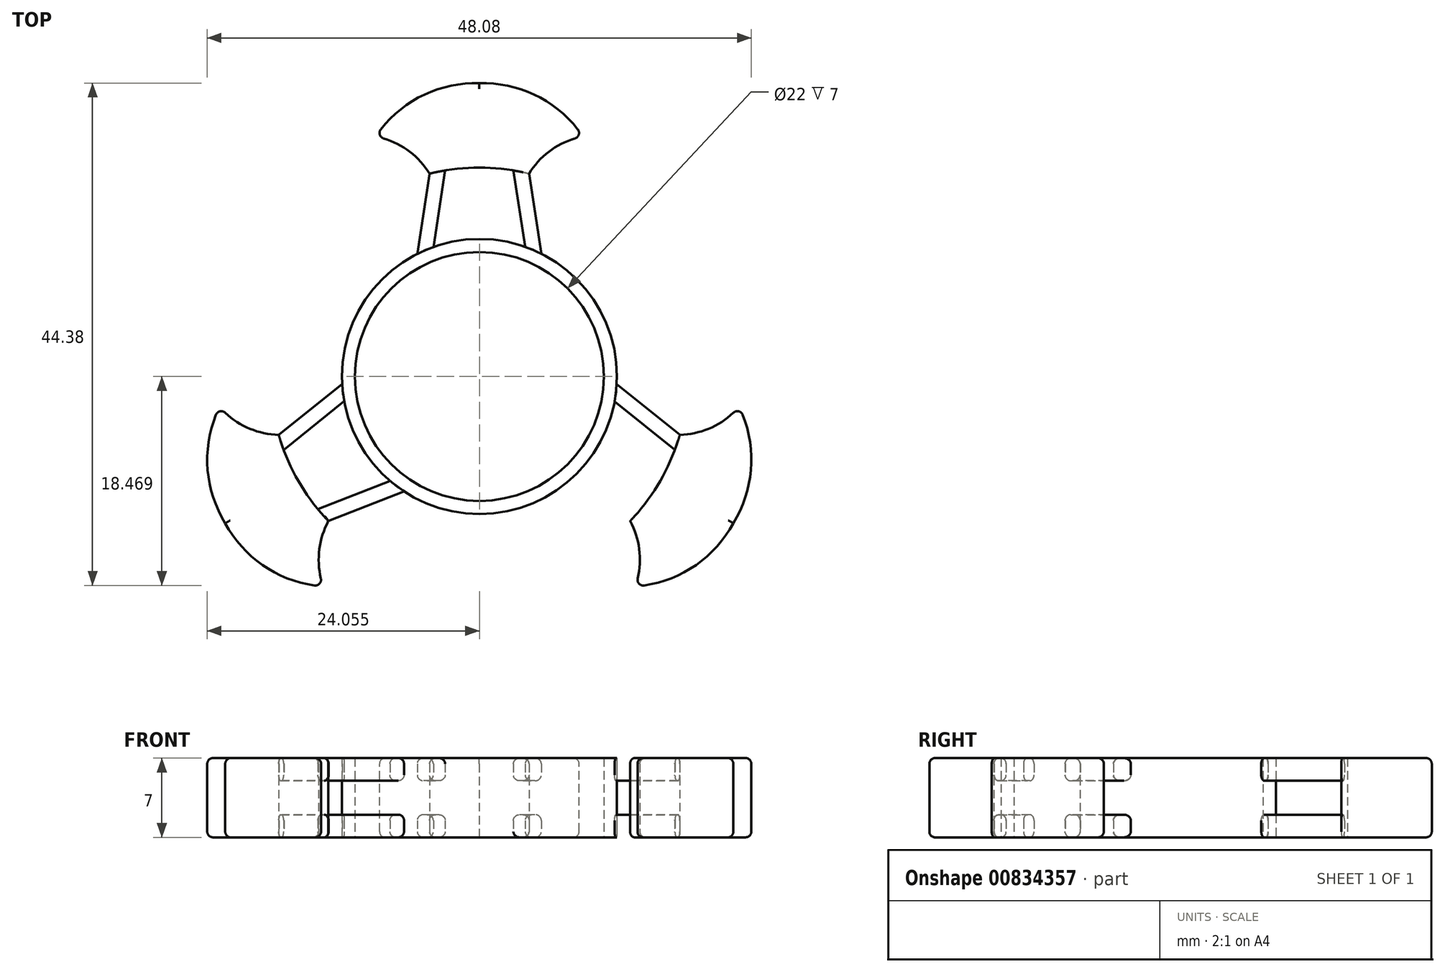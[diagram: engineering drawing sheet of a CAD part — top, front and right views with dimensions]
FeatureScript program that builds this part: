
annotation { "Feature Type Name" : "Feature", "Feature Type Description" : "" }
export const myFeature = defineFeature(function(context is Context, id is Id, definition is map)
    precondition{}
    {
        {
            var Q0;
            Q0=qCreatedBy(makeId("Top.planeOp"),FACE);
            var sketch = newSketch(context, id + "F0", { "sketchPlane" : qUnion([Q0])});
            skArc(sketch, "E0", {"start": v(9.16, 21.21) * mm, "mid": v(5.19, 24.74) * mm, "end": v(0, 25.91) * mm});
            skArc(sketch, "E1", {"start": v(9.16, 21.21) * mm, "mid": v(6.43, 20.07) * mm, "end": v(4.4, 17.93) * mm});
            skArc(sketch, "E2.MirrorCS", {"start": v(-9.16, 21.21) * mm, "mid": v(-6.43, 20.07) * mm, "end": v(-4.4, 17.93) * mm});
            skArc(sketch, "E3.MirrorCS", {"start": v(-9.16, 21.21) * mm, "mid": v(-5.19, 24.74) * mm, "end": v(0, 25.91) * mm});
            skArc(sketch, "E4", {"start": v(4.4, 17.93) * mm, "mid": v(0, 18.45) * mm, "end": v(-4.4, 17.93) * mm});
            skArc(sketch, "E5.MirrorCS", {"start": v(13.8, -18.54) * mm, "mid": v(18.84, -16.86) * mm, "end": v(22.44, -12.96) * mm});
            skArc(sketch, "E6.MirrorCS", {"start": v(22.95, -2.67) * mm, "mid": v(24.02, -7.88) * mm, "end": v(22.44, -12.96) * mm});
            skArc(sketch, "E7.MirrorCS", {"start": v(22.95, -2.67) * mm, "mid": v(20.6, -4.46) * mm, "end": v(17.72, -5.16) * mm});
            skArc(sketch, "E8.MirrorCS", {"start": v(13.8, -18.54) * mm, "mid": v(14.16, -15.6) * mm, "end": v(13.33, -12.77) * mm});
            skArc(sketch, "E9.MirrorCS", {"start": v(17.72, -5.16) * mm, "mid": v(15.98, -9.23) * mm, "end": v(13.33, -12.77) * mm});
            skArc(sketch, "E10.MirrorCS", {"start": v(-17.72, -5.16) * mm, "mid": v(-15.98, -9.23) * mm, "end": v(-13.33, -12.77) * mm});
            skArc(sketch, "E11.MirrorCS", {"start": v(-22.95, -2.67) * mm, "mid": v(-20.6, -4.46) * mm, "end": v(-17.72, -5.16) * mm});
            skArc(sketch, "E12.MirrorCS", {"start": v(-22.95, -2.67) * mm, "mid": v(-24.02, -7.88) * mm, "end": v(-22.44, -12.96) * mm});
            skArc(sketch, "E13.MirrorCS", {"start": v(-13.8, -18.54) * mm, "mid": v(-14.16, -15.6) * mm, "end": v(-13.33, -12.77) * mm});
            skArc(sketch, "E14.MirrorCS", {"start": v(-13.8, -18.54) * mm, "mid": v(-18.84, -16.86) * mm, "end": v(-22.44, -12.96) * mm});
            skLineSegment(sketch, "E15", {"start": v(8.04, -4.26) * mm, "end": v(8.02, -4.24) * mm});
            skLineSegment(sketch, "E16", {"start": v(7.72, -4.81) * mm, "end": v(7.7, -4.8) * mm});
            skLineSegment(sketch, "E17", {"start": v(-14.25, -11.7) * mm, "end": v(-14.27, -11.7) * mm});
            skLineSegment(sketch, "E18", {"start": v(9.09, 0.13) * mm, "end": v(9.06, 0.15) * mm});
            skLineSegment(sketch, "E19", {"start": v(4.64, 7.81) * mm, "end": v(4.65, 7.78) * mm});
            skCircle(sketch, "E20", {"center": v(0.01, 0) * mm, "radius": 11 * mm});
            skCircle(sketch, "E21", {"center": v(0.01, 0) * mm, "radius": 12.15 * mm});
            skLineSegment(sketch, "E22", {"start": v(-4.4, 17.93) * mm, "end": v(-5.48, 10.84) * mm});
            skLineSegment(sketch, "E23", {"start": v(-4.05, 11.45) * mm, "end": v(-3.02, 18.2) * mm});
            skLineSegment(sketch, "E24.MirrorCS", {"start": v(4.05, 11.45) * mm, "end": v(3.02, 18.2) * mm});
            skLineSegment(sketch, "E25.MirrorCS", {"start": v(4.4, 17.93) * mm, "end": v(5.48, 10.84) * mm});
            skLineSegment(sketch, "E26.MirrorCS", {"start": v(-11.93, -2.19) * mm, "end": v(-17.26, -6.47) * mm});
            skLineSegment(sketch, "E27.MirrorCS", {"start": v(-17.7, -5.13) * mm, "end": v(-12.11, -0.65) * mm});
            skLineSegment(sketch, "E28.MirrorCS", {"start": v(-7.88, -9.21) * mm, "end": v(-14.24, -11.69) * mm});
            skLineSegment(sketch, "E29.MirrorCS", {"start": v(-13.31, -12.74) * mm, "end": v(-6.63, -10.14) * mm});
            skLineSegment(sketch, "E30", {"start": v(-14.24, -11.69) * mm, "end": v(-14.25, -11.7) * mm});
            skLineSegment(sketch, "E31", {"start": v(-13.31, -12.74) * mm, "end": v(-13.33, -12.77) * mm});
            skLineSegment(sketch, "E32", {"start": v(-17.26, -6.47) * mm, "end": v(-17.28, -6.48) * mm});
            skLineSegment(sketch, "E33", {"start": v(-17.7, -5.13) * mm, "end": v(-17.72, -5.16) * mm});
            skLineSegment(sketch, "E34.MirrorCS", {"start": v(11.93, -2.19) * mm, "end": v(17.26, -6.47) * mm});
            skLineSegment(sketch, "E35.MirrorCS", {"start": v(17.7, -5.13) * mm, "end": v(12.11, -0.65) * mm});
            skLineSegment(sketch, "E36.MirrorCS", {"start": v(7.88, -9.21) * mm, "end": v(14.24, -11.69) * mm});
            skLineSegment(sketch, "E37.MirrorCS", {"start": v(13.31, -12.74) * mm, "end": v(6.63, -10.14) * mm});
            skLineSegment(sketch, "E38", {"start": v(13.31, -12.74) * mm, "end": v(13.33, -12.77) * mm});
            skLineSegment(sketch, "E39", {"start": v(14.24, -11.69) * mm, "end": v(14.26, -11.7) * mm});
            skLineSegment(sketch, "E40.MirrorCS", {"start": v(14.25, -11.7) * mm, "end": v(14.27, -11.7) * mm});
            skLineSegment(sketch, "E41.MirrorCS", {"start": v(14.24, -11.69) * mm, "end": v(14.25, -11.7) * mm});
            skLineSegment(sketch, "E42.MirrorCS", {"start": v(17.26, -6.47) * mm, "end": v(17.28, -6.48) * mm});
            skLineSegment(sketch, "E43.MirrorCS", {"start": v(17.7, -5.13) * mm, "end": v(17.72, -5.16) * mm});
            skSolve(sketch);
        }
        {
            var Q0;
            Q0=makeQuery(id+"F0.imprint","IMPRINT",FACE,{"disambiguationData":[TD([[makeQuery(id+"F0.imprint","IMPRINT",EDGE,{"derivedFrom":sQuery(id+"F0.wireOp",EDGE,"E0")}),1.0]])]});
            var Q1;
            Q1=makeQuery(id+"F0.imprint","IMPRINT",FACE,{"disambiguationData":[TD([[makeQuery(id+"F0.imprint","IMPRINT",EDGE,{"derivedFrom":sQuery(id+"F0.wireOp",EDGE,"E5.MirrorCS")}),1.0]])]});
            var Q2;
            {var subQ0=sQuery(id+"F0.wireOp",EDGE,"E11.MirrorCS");Q2=makeQuery(id+"F0.imprint","IMPRINT",FACE,{"disambiguationData":[TD([[makeQuery(id+"F0.imprint","IMPRINT",EDGE,{"derivedFrom":subQ0}),-1.0]])]});}
            var Q3;
            Q3=makeQuery(id+"F0.imprint","IMPRINT",FACE,{"disambiguationData":[TD([[makeQuery(id+"F0.imprint","IMPRINT",EDGE,{"derivedFrom":sQuery(id+"F0.wireOp",EDGE,"E20")}),-1.0]])]});
            extrude(context, id + "F1", {"entities" : qUnion([Q0, Q1, Q2, Q3]), "depth" : 7 * mm, "offsetDistance" : 25.4 * mm});
        }
        {
            var Q0;
            Q0=makeQuery(id+"F1.opExtrude","CAP_EDGE",EDGE,{"disambiguationData":[OSD([sQuery(id+"F0.wireOp",EDGE,"E2.MirrorCS")])],"isStart":false});
            var Q1;
            Q1=makeQuery(id+"F1.opExtrude","CAP_EDGE",EDGE,{"disambiguationData":[OSD([sQuery(id+"F0.wireOp",EDGE,"E2.MirrorCS")])],"isStart":true});
            var Q2;
            Q2=makeQuery(id+"F1.opExtrude","CAP_EDGE",EDGE,{"disambiguationData":[OSD([sQuery(id+"F0.wireOp",EDGE,"E3.MirrorCS")])],"isStart":false});
            var Q3;
            Q3=makeQuery(id+"F1.opExtrude","CAP_EDGE",EDGE,{"disambiguationData":[OSD([sQuery(id+"F0.wireOp",EDGE,"E3.MirrorCS")])],"isStart":true});
            var Q4;
            Q4=makeQuery(id+"F1.opExtrude","CAP_EDGE",EDGE,{"disambiguationData":[OSD([sQuery(id+"F0.wireOp",EDGE,"E0")])],"isStart":false});
            var Q5;
            Q5=makeQuery(id+"F1.opExtrude","CAP_EDGE",EDGE,{"disambiguationData":[OSD([sQuery(id+"F0.wireOp",EDGE,"E1")])],"isStart":false});
            var Q6;
            Q6=makeQuery(id+"F1.opExtrude","CAP_EDGE",EDGE,{"disambiguationData":[OSD([sQuery(id+"F0.wireOp",EDGE,"E1")])],"isStart":true});
            var Q7;
            Q7=makeQuery(id+"F1.opExtrude","CAP_EDGE",EDGE,{"disambiguationData":[OSD([sQuery(id+"F0.wireOp",EDGE,"E0")])],"isStart":true});
            var Q8;
            Q8=makeQuery(id+"F1.opExtrude","SWEPT_EDGE",EDGE,{"disambiguationData":[OSD([sQuery(id+"F0.wireOp",EDGE,"E0"),sQuery(id+"F0.wireOp",EDGE,"E1")])]});
            var Q9;
            Q9=makeQuery(id+"F1.opExtrude","SWEPT_EDGE",EDGE,{"disambiguationData":[OSD([sQuery(id+"F0.wireOp",EDGE,"E2.MirrorCS"),sQuery(id+"F0.wireOp",EDGE,"E3.MirrorCS")])]});
            var Q10;
            Q10=makeQuery(id+"F1.opExtrude","CAP_EDGE",EDGE,{"disambiguationData":[OSD([sQuery(id+"F0.wireOp",EDGE,"E7.MirrorCS")])],"isStart":false});
            var Q11;
            Q11=makeQuery(id+"F1.opExtrude","CAP_EDGE",EDGE,{"disambiguationData":[OSD([sQuery(id+"F0.wireOp",EDGE,"E6.MirrorCS")])],"isStart":false});
            var Q12;
            Q12=makeQuery(id+"F1.opExtrude","CAP_EDGE",EDGE,{"disambiguationData":[OSD([sQuery(id+"F0.wireOp",EDGE,"E5.MirrorCS")])],"isStart":false});
            var Q13;
            Q13=makeQuery(id+"F1.opExtrude","CAP_EDGE",EDGE,{"disambiguationData":[OSD([sQuery(id+"F0.wireOp",EDGE,"E8.MirrorCS")])],"isStart":false});
            var Q14;
            Q14=makeQuery(id+"F1.opExtrude","SWEPT_EDGE",EDGE,{"disambiguationData":[OSD([sQuery(id+"F0.wireOp",EDGE,"E5.MirrorCS"),sQuery(id+"F0.wireOp",EDGE,"E8.MirrorCS")])]});
            var Q15;
            Q15=makeQuery(id+"F1.opExtrude","SWEPT_EDGE",EDGE,{"disambiguationData":[OSD([sQuery(id+"F0.wireOp",EDGE,"E6.MirrorCS"),sQuery(id+"F0.wireOp",EDGE,"E7.MirrorCS")])]});
            var Q16;
            Q16=makeQuery(id+"F1.opExtrude","CAP_EDGE",EDGE,{"disambiguationData":[OSD([sQuery(id+"F0.wireOp",EDGE,"E7.MirrorCS")])],"isStart":true});
            var Q17;
            Q17=makeQuery(id+"F1.opExtrude","CAP_EDGE",EDGE,{"disambiguationData":[OSD([sQuery(id+"F0.wireOp",EDGE,"E6.MirrorCS")])],"isStart":true});
            var Q18;
            Q18=makeQuery(id+"F1.opExtrude","CAP_EDGE",EDGE,{"disambiguationData":[OSD([sQuery(id+"F0.wireOp",EDGE,"E8.MirrorCS")])],"isStart":true});
            var Q19;
            Q19=makeQuery(id+"F1.opExtrude","CAP_EDGE",EDGE,{"disambiguationData":[OSD([sQuery(id+"F0.wireOp",EDGE,"E5.MirrorCS")])],"isStart":true});
            var Q20;
            Q20=makeQuery(id+"F1.opExtrude","CAP_EDGE",EDGE,{"disambiguationData":[OSD([sQuery(id+"F0.wireOp",EDGE,"E11.MirrorCS")])],"isStart":false});
            var Q21;
            Q21=makeQuery(id+"F1.opExtrude","CAP_EDGE",EDGE,{"disambiguationData":[OSD([sQuery(id+"F0.wireOp",EDGE,"E12.MirrorCS")])],"isStart":false});
            var Q22;
            Q22=makeQuery(id+"F1.opExtrude","CAP_EDGE",EDGE,{"disambiguationData":[OSD([sQuery(id+"F0.wireOp",EDGE,"E14.MirrorCS")])],"isStart":false});
            var Q23;
            Q23=makeQuery(id+"F1.opExtrude","CAP_EDGE",EDGE,{"disambiguationData":[OSD([sQuery(id+"F0.wireOp",EDGE,"E13.MirrorCS")])],"isStart":false});
            var Q24;
            Q24=makeQuery(id+"F1.opExtrude","SWEPT_EDGE",EDGE,{"disambiguationData":[OSD([sQuery(id+"F0.wireOp",EDGE,"E13.MirrorCS"),sQuery(id+"F0.wireOp",EDGE,"E14.MirrorCS")])]});
            var Q25;
            Q25=makeQuery(id+"F1.opExtrude","CAP_EDGE",EDGE,{"disambiguationData":[OSD([sQuery(id+"F0.wireOp",EDGE,"E13.MirrorCS")])],"isStart":true});
            var Q26;
            Q26=makeQuery(id+"F1.opExtrude","SWEPT_EDGE",EDGE,{"disambiguationData":[OSD([sQuery(id+"F0.wireOp",EDGE,"E11.MirrorCS"),sQuery(id+"F0.wireOp",EDGE,"E12.MirrorCS")])]});
            var Q27;
            Q27=makeQuery(id+"F1.opExtrude","CAP_EDGE",EDGE,{"disambiguationData":[OSD([sQuery(id+"F0.wireOp",EDGE,"E11.MirrorCS")])],"isStart":true});
            var Q28;
            Q28=makeQuery(id+"F1.opExtrude","CAP_EDGE",EDGE,{"disambiguationData":[OSD([sQuery(id+"F0.wireOp",EDGE,"E12.MirrorCS")])],"isStart":true});
            var Q29;
            Q29=makeQuery(id+"F1.opExtrude","CAP_EDGE",EDGE,{"disambiguationData":[OSD([sQuery(id+"F0.wireOp",EDGE,"E14.MirrorCS")])],"isStart":true});
            fillet(context, id + "F2", {"entities" : qUnion([Q0, Q1, Q2, Q3, Q4, Q5, Q6, Q7, Q8, Q9, Q10, Q11, Q12, Q13, Q14, Q15, Q16, Q17, Q18, Q19, Q20, Q21, Q22, Q23, Q24, Q25, Q26, Q27, Q28, Q29]), "radius" : 0.5 * mm, "tangentPropagation" : true, "allowEdgeOverflow" : false});
        }
        {
            var Q0;
            {var subQ0=sQuery(id+"F0.wireOp",EDGE,"E22");Q0=makeQuery(id+"F0.imprint","IMPRINT",FACE,{"disambiguationData":[TD([[makeQuery(id+"F0.imprint","IMPRINT",EDGE,{"derivedFrom":subQ0}),1.0]])]});}
            var Q1;
            {var subQ0=sQuery(id+"F0.wireOp",EDGE,"E25.MirrorCS");var subQ5=sQuery(id+"F0.wireOp",EDGE,"E21");var subQ6=makeQuery(id+"F0.imprint","INTERSECT",VERTEX,{"derivedFrom":[subQ5,subQ0]});Q1=makeQuery(id+"F0.imprint","IMPRINT",FACE,{"disambiguationData":[TD([[makeQuery(id+"F0.imprint","IMPRINT",EDGE,{"disambiguationData":[TD([[subQ6,-1.0]])],"derivedFrom":subQ5}),-1.0]])]});}
            var Q2;
            {var subQ1=sQuery(id+"F0.wireOp",EDGE,"E26.MirrorCS");Q2=makeQuery(id+"F0.imprint","IMPRINT",FACE,{"disambiguationData":[TD([[makeQuery(id+"F0.imprint","IMPRINT",EDGE,{"derivedFrom":subQ1}),-1.0]])]});}
            var Q3;
            {var subQ6=sQuery(id+"F0.wireOp",EDGE,"E17");Q3=makeQuery(id+"F0.imprint","IMPRINT",FACE,{"disambiguationData":[TD([[makeQuery(id+"F0.imprint","IMPRINT",EDGE,{"derivedFrom":subQ6}),1.0]])]});}
            var Q4;
            {var subQ0=sQuery(id+"F0.wireOp",EDGE,"E42.MirrorCS");Q4=makeQuery(id+"F0.imprint","IMPRINT",FACE,{"disambiguationData":[TD([[makeQuery(id+"F0.imprint","IMPRINT",EDGE,{"derivedFrom":subQ0}),1.0]])]});}
            var Q5;
            {var subQ0=sQuery(id+"F0.wireOp",EDGE,"E38");Q5=makeQuery(id+"F0.imprint","IMPRINT",FACE,{"disambiguationData":[TD([[makeQuery(id+"F0.imprint","IMPRINT",EDGE,{"derivedFrom":subQ0}),1.0]])]});}
            extrude(context, id + "F3", {"entities" : qUnion([Q0, Q1, Q2, Q3, Q4, Q5]), "depth" : 2 * mm, "offsetDistance" : 25.4 * mm});
        }
        {
            var Q0;
            Q0=makeQuery(id+"F3.opExtrude","SWEPT_BODY",BODY,{"disambiguationData":[OSD([sQuery(id+"F0.wireOp",EDGE,"E9.MirrorCS"),sQuery(id+"F0.wireOp",EDGE,"E21"),sQuery(id+"F0.wireOp",EDGE,"E36.MirrorCS"),sQuery(id+"F0.wireOp",EDGE,"E37.MirrorCS"),sQuery(id+"F0.wireOp",EDGE,"E38"),sQuery(id+"F0.wireOp",EDGE,"E40.MirrorCS"),sQuery(id+"F0.wireOp",EDGE,"E41.MirrorCS")])]});
            var Q1;
            Q1=makeQuery(id+"F3.opExtrude","SWEPT_BODY",BODY,{"disambiguationData":[OSD([sQuery(id+"F0.wireOp",EDGE,"E10.MirrorCS"),sQuery(id+"F0.wireOp",EDGE,"E17"),sQuery(id+"F0.wireOp",EDGE,"E21"),sQuery(id+"F0.wireOp",EDGE,"E28.MirrorCS"),sQuery(id+"F0.wireOp",EDGE,"E29.MirrorCS"),sQuery(id+"F0.wireOp",EDGE,"E30"),sQuery(id+"F0.wireOp",EDGE,"E31")])]});
            var Q2;
            Q2=makeQuery(id+"F3.opExtrude","SWEPT_BODY",BODY,{"disambiguationData":[OSD([sQuery(id+"F0.wireOp",EDGE,"E10.MirrorCS"),sQuery(id+"F0.wireOp",EDGE,"E21"),sQuery(id+"F0.wireOp",EDGE,"E26.MirrorCS"),sQuery(id+"F0.wireOp",EDGE,"E27.MirrorCS"),sQuery(id+"F0.wireOp",EDGE,"E32"),sQuery(id+"F0.wireOp",EDGE,"E33")])]});
            var Q3;
            Q3=makeQuery(id+"F3.opExtrude","SWEPT_BODY",BODY,{"disambiguationData":[OSD([sQuery(id+"F0.wireOp",EDGE,"E9.MirrorCS"),sQuery(id+"F0.wireOp",EDGE,"E21"),sQuery(id+"F0.wireOp",EDGE,"E34.MirrorCS"),sQuery(id+"F0.wireOp",EDGE,"E35.MirrorCS"),sQuery(id+"F0.wireOp",EDGE,"E42.MirrorCS"),sQuery(id+"F0.wireOp",EDGE,"E43.MirrorCS")])]});
            var Q4;
            Q4=makeQuery(id+"F3.opExtrude","SWEPT_BODY",BODY,{"disambiguationData":[OSD([sQuery(id+"F0.wireOp",EDGE,"E4"),sQuery(id+"F0.wireOp",EDGE,"E21"),sQuery(id+"F0.wireOp",EDGE,"E24.MirrorCS"),sQuery(id+"F0.wireOp",EDGE,"E25.MirrorCS")])]});
            var Q5;
            Q5=makeQuery(id+"F3.opExtrude","SWEPT_BODY",BODY,{"disambiguationData":[OSD([sQuery(id+"F0.wireOp",EDGE,"E4"),sQuery(id+"F0.wireOp",EDGE,"E21"),sQuery(id+"F0.wireOp",EDGE,"E22"),sQuery(id+"F0.wireOp",EDGE,"E23")])]});
            transform(context, id + "F4", {"entities" : qUnion([Q0, Q1, Q2, Q3, Q4, Q5]), "transformType" : TransformType.TRANSLATION_3D, "dx" : 0 * mm, "dy" : 0 * mm, "dz" : 5 * mm, "makeCopy" : false});
        }
        {
            var Q0;
            {var subQ0=sQuery(id+"F0.wireOp",EDGE,"E42.MirrorCS");Q0=makeQuery(id+"F0.imprint","IMPRINT",FACE,{"disambiguationData":[TD([[makeQuery(id+"F0.imprint","IMPRINT",EDGE,{"derivedFrom":subQ0}),1.0]])]});}
            var Q1;
            {var subQ0=sQuery(id+"F0.wireOp",EDGE,"E38");Q1=makeQuery(id+"F0.imprint","IMPRINT",FACE,{"disambiguationData":[TD([[makeQuery(id+"F0.imprint","IMPRINT",EDGE,{"derivedFrom":subQ0}),1.0]])]});}
            var Q2;
            {var subQ6=sQuery(id+"F0.wireOp",EDGE,"E17");Q2=makeQuery(id+"F0.imprint","IMPRINT",FACE,{"disambiguationData":[TD([[makeQuery(id+"F0.imprint","IMPRINT",EDGE,{"derivedFrom":subQ6}),1.0]])]});}
            var Q3;
            {var subQ1=sQuery(id+"F0.wireOp",EDGE,"E26.MirrorCS");Q3=makeQuery(id+"F0.imprint","IMPRINT",FACE,{"disambiguationData":[TD([[makeQuery(id+"F0.imprint","IMPRINT",EDGE,{"derivedFrom":subQ1}),-1.0]])]});}
            var Q4;
            {var subQ0=sQuery(id+"F0.wireOp",EDGE,"E25.MirrorCS");var subQ5=sQuery(id+"F0.wireOp",EDGE,"E21");var subQ6=makeQuery(id+"F0.imprint","INTERSECT",VERTEX,{"derivedFrom":[subQ5,subQ0]});Q4=makeQuery(id+"F0.imprint","IMPRINT",FACE,{"disambiguationData":[TD([[makeQuery(id+"F0.imprint","IMPRINT",EDGE,{"disambiguationData":[TD([[subQ6,-1.0]])],"derivedFrom":subQ5}),-1.0]])]});}
            var Q5;
            {var subQ0=sQuery(id+"F0.wireOp",EDGE,"E22");Q5=makeQuery(id+"F0.imprint","IMPRINT",FACE,{"disambiguationData":[TD([[makeQuery(id+"F0.imprint","IMPRINT",EDGE,{"derivedFrom":subQ0}),1.0]])]});}
            extrude(context, id + "F5", {"entities" : qUnion([Q0, Q1, Q2, Q3, Q4, Q5]), "depth" : 2 * mm, "offsetDistance" : 25.4 * mm});
        }
        {
            var Q0;
            Q0=makeQuery(id+"F3.opExtrude","CAP_EDGE",EDGE,{"disambiguationData":[OSD([sQuery(id+"F0.wireOp",EDGE,"E24.MirrorCS")])],"isStart":true});
            var Q1;
            Q1=makeQuery(id+"F3.opExtrude","CAP_EDGE",EDGE,{"disambiguationData":[OSD([sQuery(id+"F0.wireOp",EDGE,"E24.MirrorCS")])],"isStart":false});
            var Q2;
            Q2=makeQuery(id+"F3.opExtrude","CAP_EDGE",EDGE,{"disambiguationData":[OSD([sQuery(id+"F0.wireOp",EDGE,"E25.MirrorCS")])],"isStart":false});
            var Q3;
            Q3=makeQuery(id+"F3.opExtrude","CAP_EDGE",EDGE,{"disambiguationData":[OSD([sQuery(id+"F0.wireOp",EDGE,"E25.MirrorCS")])],"isStart":true});
            var Q4;
            Q4=makeQuery(id+"F5.opExtrude","CAP_EDGE",EDGE,{"disambiguationData":[OSD([sQuery(id+"F0.wireOp",EDGE,"E24.MirrorCS")])],"isStart":false});
            var Q5;
            Q5=makeQuery(id+"F5.opExtrude","CAP_EDGE",EDGE,{"disambiguationData":[OSD([sQuery(id+"F0.wireOp",EDGE,"E25.MirrorCS")])],"isStart":false});
            var Q6;
            Q6=makeQuery(id+"F3.opExtrude","CAP_EDGE",EDGE,{"disambiguationData":[OSD([sQuery(id+"F0.wireOp",EDGE,"E22")])],"isStart":true});
            var Q7;
            Q7=makeQuery(id+"F3.opExtrude","CAP_EDGE",EDGE,{"disambiguationData":[OSD([sQuery(id+"F0.wireOp",EDGE,"E22")])],"isStart":false});
            var Q8;
            Q8=makeQuery(id+"F3.opExtrude","CAP_EDGE",EDGE,{"disambiguationData":[OSD([sQuery(id+"F0.wireOp",EDGE,"E23")])],"isStart":false});
            var Q9;
            Q9=makeQuery(id+"F3.opExtrude","CAP_EDGE",EDGE,{"disambiguationData":[OSD([sQuery(id+"F0.wireOp",EDGE,"E23")])],"isStart":true});
            var Q10;
            Q10=makeQuery(id+"F5.opExtrude","CAP_EDGE",EDGE,{"disambiguationData":[OSD([sQuery(id+"F0.wireOp",EDGE,"E22")])],"isStart":false});
            var Q11;
            Q11=makeQuery(id+"F5.opExtrude","CAP_EDGE",EDGE,{"disambiguationData":[OSD([sQuery(id+"F0.wireOp",EDGE,"E37.MirrorCS")])],"isStart":false});
            var Q12;
            Q12=makeQuery(id+"F3.opExtrude","CAP_EDGE",EDGE,{"disambiguationData":[OSD([sQuery(id+"F0.wireOp",EDGE,"E37.MirrorCS")])],"isStart":false});
            var Q13;
            Q13=makeQuery(id+"F3.opExtrude","CAP_EDGE",EDGE,{"disambiguationData":[OSD([sQuery(id+"F0.wireOp",EDGE,"E37.MirrorCS")])],"isStart":true});
            var Q14;
            Q14=makeQuery(id+"F5.opExtrude","CAP_EDGE",EDGE,{"disambiguationData":[OSD([sQuery(id+"F0.wireOp",EDGE,"E34.MirrorCS")])],"isStart":false});
            var Q15;
            Q15=makeQuery(id+"F3.opExtrude","CAP_EDGE",EDGE,{"disambiguationData":[OSD([sQuery(id+"F0.wireOp",EDGE,"E36.MirrorCS")])],"isStart":false});
            var Q16;
            Q16=makeQuery(id+"F3.opExtrude","CAP_EDGE",EDGE,{"disambiguationData":[OSD([sQuery(id+"F0.wireOp",EDGE,"E36.MirrorCS")])],"isStart":true});
            var Q17;
            Q17=makeQuery(id+"F5.opExtrude","CAP_EDGE",EDGE,{"disambiguationData":[OSD([sQuery(id+"F0.wireOp",EDGE,"E36.MirrorCS")])],"isStart":false});
            var Q18;
            Q18=makeQuery(id+"F3.opExtrude","CAP_EDGE",EDGE,{"disambiguationData":[OSD([sQuery(id+"F0.wireOp",EDGE,"E35.MirrorCS")])],"isStart":true});
            var Q19;
            Q19=makeQuery(id+"F3.opExtrude","CAP_EDGE",EDGE,{"disambiguationData":[OSD([sQuery(id+"F0.wireOp",EDGE,"E35.MirrorCS")])],"isStart":false});
            var Q20;
            Q20=makeQuery(id+"F5.opExtrude","CAP_EDGE",EDGE,{"disambiguationData":[OSD([sQuery(id+"F0.wireOp",EDGE,"E35.MirrorCS")])],"isStart":false});
            var Q21;
            Q21=makeQuery(id+"F3.opExtrude","CAP_EDGE",EDGE,{"disambiguationData":[OSD([sQuery(id+"F0.wireOp",EDGE,"E34.MirrorCS")])],"isStart":true});
            var Q22;
            Q22=makeQuery(id+"F3.opExtrude","CAP_EDGE",EDGE,{"disambiguationData":[OSD([sQuery(id+"F0.wireOp",EDGE,"E34.MirrorCS")])],"isStart":false});
            var Q23;
            Q23=makeQuery(id+"F3.opExtrude","CAP_EDGE",EDGE,{"disambiguationData":[OSD([sQuery(id+"F0.wireOp",EDGE,"E29.MirrorCS")])],"isStart":false});
            var Q24;
            Q24=makeQuery(id+"F3.opExtrude","CAP_EDGE",EDGE,{"disambiguationData":[OSD([sQuery(id+"F0.wireOp",EDGE,"E28.MirrorCS")])],"isStart":false});
            var Q25;
            Q25=makeQuery(id+"F3.opExtrude","CAP_EDGE",EDGE,{"disambiguationData":[OSD([sQuery(id+"F0.wireOp",EDGE,"E27.MirrorCS")])],"isStart":false});
            var Q26;
            Q26=makeQuery(id+"F3.opExtrude","CAP_EDGE",EDGE,{"disambiguationData":[OSD([sQuery(id+"F0.wireOp",EDGE,"E26.MirrorCS")])],"isStart":false});
            var Q27;
            Q27=makeQuery(id+"F5.opExtrude","CAP_EDGE",EDGE,{"disambiguationData":[OSD([sQuery(id+"F0.wireOp",EDGE,"E28.MirrorCS")])],"isStart":false});
            var Q28;
            Q28=makeQuery(id+"F5.opExtrude","CAP_EDGE",EDGE,{"disambiguationData":[OSD([sQuery(id+"F0.wireOp",EDGE,"E29.MirrorCS")])],"isStart":false});
            var Q29;
            Q29=makeQuery(id+"F3.opExtrude","CAP_EDGE",EDGE,{"disambiguationData":[OSD([sQuery(id+"F0.wireOp",EDGE,"E28.MirrorCS")])],"isStart":true});
            var Q30;
            Q30=makeQuery(id+"F3.opExtrude","CAP_EDGE",EDGE,{"disambiguationData":[OSD([sQuery(id+"F0.wireOp",EDGE,"E29.MirrorCS")])],"isStart":true});
            var Q31;
            Q31=makeQuery(id+"F5.opExtrude","CAP_EDGE",EDGE,{"disambiguationData":[OSD([sQuery(id+"F0.wireOp",EDGE,"E27.MirrorCS")])],"isStart":false});
            var Q32;
            Q32=makeQuery(id+"F3.opExtrude","CAP_EDGE",EDGE,{"disambiguationData":[OSD([sQuery(id+"F0.wireOp",EDGE,"E26.MirrorCS")])],"isStart":true});
            var Q33;
            Q33=makeQuery(id+"F5.opExtrude","CAP_EDGE",EDGE,{"disambiguationData":[OSD([sQuery(id+"F0.wireOp",EDGE,"E26.MirrorCS")])],"isStart":false});
            var Q34;
            Q34=makeQuery(id+"F3.opExtrude","CAP_EDGE",EDGE,{"disambiguationData":[OSD([sQuery(id+"F0.wireOp",EDGE,"E27.MirrorCS")])],"isStart":true});
            var Q35;
            Q35=makeQuery(id+"F3.opExtrude","CAP_EDGE",EDGE,{"disambiguationData":[OSD([sQuery(id+"F0.wireOp",EDGE,"E38")])],"isStart":false});
            var Q36;
            Q36=makeQuery(id+"F5.opExtrude","CAP_EDGE",EDGE,{"disambiguationData":[OSD([sQuery(id+"F0.wireOp",EDGE,"E38")])],"isStart":false});
            var Q37;
            Q37=makeQuery(id+"F5.opExtrude","CAP_EDGE",EDGE,{"disambiguationData":[OSD([sQuery(id+"F0.wireOp",EDGE,"E36.MirrorCS")])],"isStart":true});
            var Q38;
            Q38=makeQuery(id+"F5.opExtrude","CAP_EDGE",EDGE,{"disambiguationData":[OSD([sQuery(id+"F0.wireOp",EDGE,"E37.MirrorCS")])],"isStart":true});
            var Q39;
            Q39=makeQuery(id+"F5.opExtrude","CAP_EDGE",EDGE,{"disambiguationData":[OSD([sQuery(id+"F0.wireOp",EDGE,"E38")])],"isStart":true});
            var Q40;
            Q40=makeQuery(id+"F3.opExtrude","CAP_EDGE",EDGE,{"disambiguationData":[OSD([sQuery(id+"F0.wireOp",EDGE,"E38")])],"isStart":true});
            var Q41;
            Q41=makeQuery(id+"F5.opExtrude","CAP_EDGE",EDGE,{"disambiguationData":[OSD([sQuery(id+"F0.wireOp",EDGE,"E34.MirrorCS")])],"isStart":true});
            var Q42;
            Q42=makeQuery(id+"F5.opExtrude","CAP_EDGE",EDGE,{"disambiguationData":[OSD([sQuery(id+"F0.wireOp",EDGE,"E35.MirrorCS")])],"isStart":true});
            var Q43;
            Q43=makeQuery(id+"F5.opExtrude","CAP_EDGE",EDGE,{"disambiguationData":[OSD([sQuery(id+"F0.wireOp",EDGE,"E29.MirrorCS")])],"isStart":true});
            var Q44;
            Q44=makeQuery(id+"F5.opExtrude","CAP_EDGE",EDGE,{"disambiguationData":[OSD([sQuery(id+"F0.wireOp",EDGE,"E28.MirrorCS")])],"isStart":true});
            var Q45;
            Q45=makeQuery(id+"F5.opExtrude","CAP_EDGE",EDGE,{"disambiguationData":[OSD([sQuery(id+"F0.wireOp",EDGE,"E31")])],"isStart":false});
            var Q46;
            Q46=makeQuery(id+"F5.opExtrude","CAP_EDGE",EDGE,{"disambiguationData":[OSD([sQuery(id+"F0.wireOp",EDGE,"E31")])],"isStart":true});
            var Q47;
            Q47=makeQuery(id+"F3.opExtrude","CAP_EDGE",EDGE,{"disambiguationData":[OSD([sQuery(id+"F0.wireOp",EDGE,"E31")])],"isStart":false});
            var Q48;
            Q48=makeQuery(id+"F3.opExtrude","CAP_EDGE",EDGE,{"disambiguationData":[OSD([sQuery(id+"F0.wireOp",EDGE,"E31")])],"isStart":true});
            var Q49;
            Q49=makeQuery(id+"F5.opExtrude","CAP_EDGE",EDGE,{"disambiguationData":[OSD([sQuery(id+"F0.wireOp",EDGE,"E27.MirrorCS")])],"isStart":true});
            var Q50;
            Q50=makeQuery(id+"F5.opExtrude","CAP_EDGE",EDGE,{"disambiguationData":[OSD([sQuery(id+"F0.wireOp",EDGE,"E26.MirrorCS")])],"isStart":true});
            var Q51;
            Q51=makeQuery(id+"F5.opExtrude","CAP_EDGE",EDGE,{"disambiguationData":[OSD([sQuery(id+"F0.wireOp",EDGE,"E23")])],"isStart":true});
            var Q52;
            Q52=makeQuery(id+"F5.opExtrude","CAP_EDGE",EDGE,{"disambiguationData":[OSD([sQuery(id+"F0.wireOp",EDGE,"E22")])],"isStart":true});
            var Q53;
            Q53=makeQuery(id+"F5.opExtrude","CAP_EDGE",EDGE,{"disambiguationData":[OSD([sQuery(id+"F0.wireOp",EDGE,"E23")])],"isStart":false});
            var Q54;
            Q54=makeQuery(id+"F5.opExtrude","CAP_EDGE",EDGE,{"disambiguationData":[OSD([sQuery(id+"F0.wireOp",EDGE,"E25.MirrorCS")])],"isStart":true});
            var Q55;
            Q55=makeQuery(id+"F5.opExtrude","CAP_EDGE",EDGE,{"disambiguationData":[OSD([sQuery(id+"F0.wireOp",EDGE,"E24.MirrorCS")])],"isStart":true});
            fillet(context, id + "F6", {"entities" : qUnion([Q0, Q1, Q2, Q3, Q4, Q5, Q6, Q7, Q8, Q9, Q10, Q11, Q12, Q13, Q14, Q15, Q16, Q17, Q18, Q19, Q20, Q21, Q22, Q23, Q24, Q25, Q26, Q27, Q28, Q29, Q30, Q31, Q32, Q33, Q34, Q35, Q36, Q37, Q38, Q39, Q40, Q41, Q42, Q43, Q44, Q45, Q46, Q47, Q48, Q49, Q50, Q51, Q52, Q53, Q54, Q55]), "radius" : 0.5 * mm, "tangentPropagation" : true, "allowEdgeOverflow" : false});
        }
    });
